# Revit family: Haworth_BuzziNordic_ST100_Sofa
name_source: partatom
category: Furniture
revit_build: Autodesk Revit 2018 (Build: 20170223_1515(x64)
units: mm (PartAtom-declared; Revit-internal decimal feet)

## family parameters
Always vertical = Yes
Cut with Voids When Loaded = No
Room Calculation Point = No
Shared = No
Work Plane-Based = No

## types (2) — shared parameters
Actual Depth = 30.71 "
Actual Height = 31.89 "
Assembly Code = E2020200
Manufacturer = Haworth
Model = HCBZ-N1L
Note = Verify Final Dim. w/ Haworth
Revision = 1
Seat Height = 16.54 "
URL = http://www.haworth.com
URL - Product = https://www.haworth.com
Warranty = http://www.haworth.com

## per-type parameters (varying)
| type | Actual Width | Back Support Width | Description | Seat Offset | Seat Width | Spindle 2S Offset | Spindle 3S Offset | Three Seats | Two Seats |
| HCBZ-N1L3 - Three Seats | 73.03 " | 68.28 " | Haworth BuzziNordic Sofa Three Seats | 11.16 " | 22.31 " | 6.83 " | 4.55 " | Yes | No |
| HCBZ-N1L2 - Two Seats | 50.59 " | 45.84 " | Haworth BuzziNordic Sofa Two Seats | 0 " | 22.25 " | 4.58 " | 3.06 " | No | Yes |

## geometry (parser evidence)
native form markers: Sweep x10
no freeform markers — native parametric forms only
